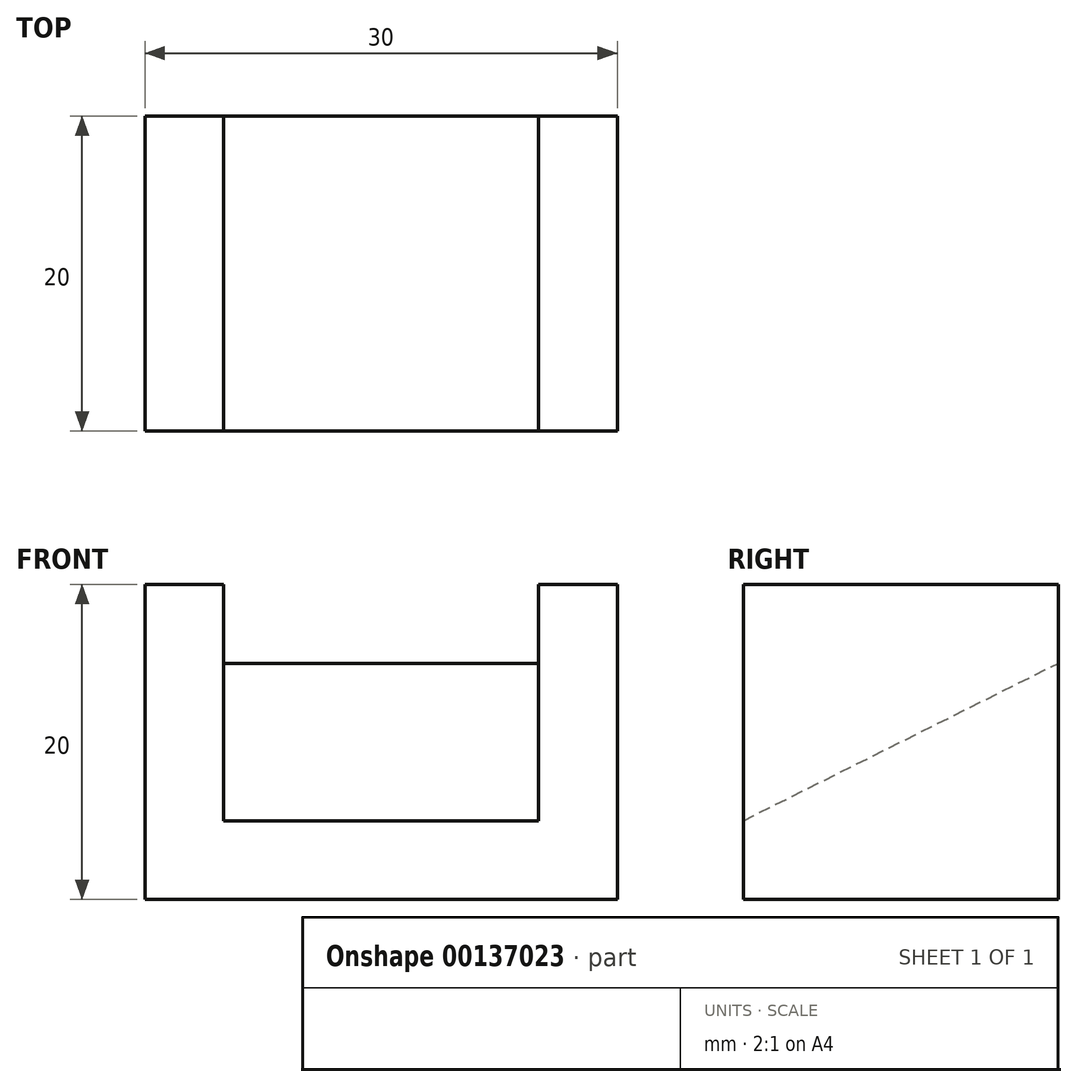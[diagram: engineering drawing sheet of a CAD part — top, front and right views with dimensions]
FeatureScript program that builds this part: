
annotation { "Feature Type Name" : "Feature", "Feature Type Description" : "" }
export const myFeature = defineFeature(function(context is Context, id is Id, definition is map)
    precondition{}
    {
        {
            var Q0;
            Q0=qCreatedBy(makeId("Right.planeOp"),FACE);
            var sketch = newSketch(context, id + "F0", { "sketchPlane" : qUnion([Q0])});
            skLineSegment(sketch, "E0.bottom", {"start": v(0, 0) * mm, "end": v(20, 0) * mm});
            skLineSegment(sketch, "E0.top", {"start": v(0, 20) * mm, "end": v(20, 20) * mm});
            skLineSegment(sketch, "E0.left", {"start": v(0, 0) * mm, "end": v(0, 20) * mm});
            skLineSegment(sketch, "E0.right", {"start": v(20, 0) * mm, "end": v(20, 20) * mm});
            skLineSegment(sketch, "E1", {"start": v(0, 5) * mm, "end": v(20, 15) * mm});
            skSolve(sketch);
        }
        {
            var Q0;
            {var subQ0=sQuery(id+"F0.wireOp",EDGE,"E0.bottom");Q0=makeQuery(id+"F0.imprint","IMPRINT",FACE,{"disambiguationData":[TD([[makeQuery(id+"F0.imprint","IMPRINT",EDGE,{"derivedFrom":subQ0}),1.0]])]});}
            extrude(context, id + "F1", {"entities" : qUnion([Q0]), "endBound" : BoundingType.SYMMETRIC, "depth" : 30 * mm});
        }
        {
            var Q0;
            {var subQ0=sQuery(id+"F0.wireOp",EDGE,"E0.top");Q0=makeQuery(id+"F0.imprint","IMPRINT",FACE,{"disambiguationData":[TD([[makeQuery(id+"F0.imprint","IMPRINT",EDGE,{"derivedFrom":subQ0}),-1.0]])]});}
            extrude(context, id + "F2", {"entities" : qUnion([Q0]), "operationType" : NewBodyOperationType.ADD, "endBound" : BoundingType.SYMMETRIC, "oppositeDirection" : true, "depth" : 30 * mm});
        }
        {
            var Q0;
            {var subQ0=sQuery(id+"F0.wireOp",EDGE,"E0.top");Q0=makeQuery(id+"F0.imprint","IMPRINT",FACE,{"disambiguationData":[TD([[makeQuery(id+"F0.imprint","IMPRINT",EDGE,{"derivedFrom":subQ0}),-1.0]])]});}
            extrude(context, id + "F3", {"entities" : qUnion([Q0]), "operationType" : NewBodyOperationType.REMOVE, "endBound" : BoundingType.SYMMETRIC, "depth" : 20 * mm});
        }
    });
